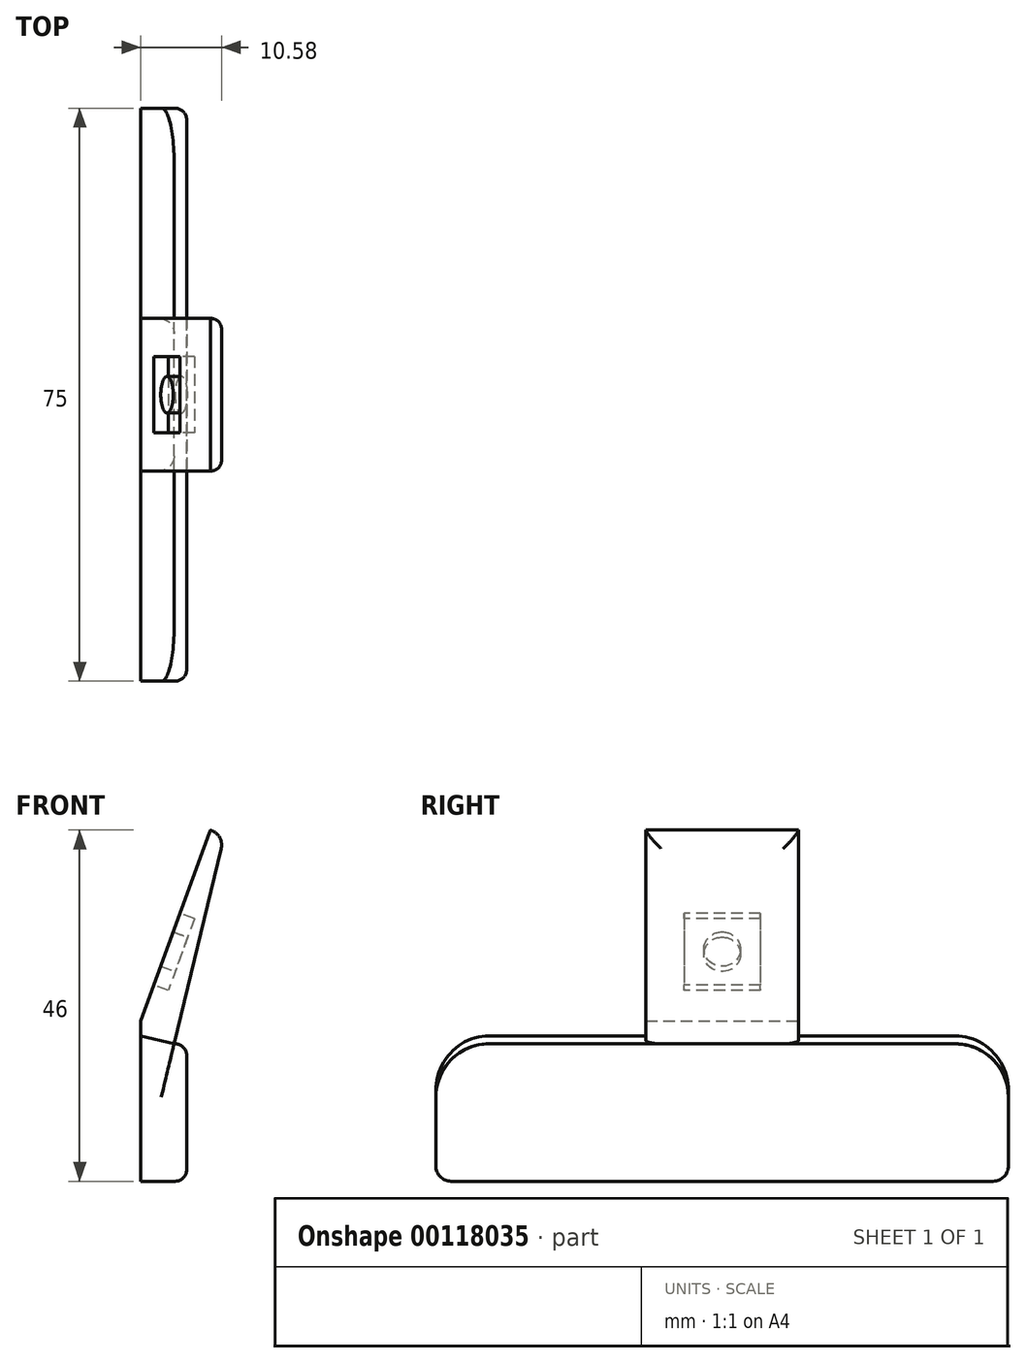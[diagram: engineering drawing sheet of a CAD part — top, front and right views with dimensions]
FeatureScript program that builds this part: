
annotation { "Feature Type Name" : "Feature", "Feature Type Description" : "" }
export const myFeature = defineFeature(function(context is Context, id is Id, definition is map)
    precondition{}
    {
        {
            var Q0;
            Q0=qCreatedBy(makeId("Right.planeOp"),FACE);
            var sketch = newSketch(context, id + "F0", { "sketchPlane" : qUnion([Q0])});
            skLineSegment(sketch, "E0", {"start": v(35.5, 0) * mm, "end": v(-35.5, 0) * mm});
            skLineSegment(sketch, "E1", {"start": v(-37.5, 2) * mm, "end": v(-37.5, 11) * mm});
            skLineSegment(sketch, "E2", {"start": v(-30.5, 18) * mm, "end": v(30.5, 18) * mm});
            skLineSegment(sketch, "E3", {"start": v(37.5, 11) * mm, "end": v(37.5, 2) * mm});
            skPoint(sketch, "E4.visualSharp", {"position": v(-37.5, 18) * mm});
            skArc(sketch, "E4.filletArc", {"start": v(-30.5, 18) * mm, "mid": v(-35.45, 15.95) * mm, "end": v(-37.5, 11) * mm});
            skPoint(sketch, "E5.visualSharp", {"position": v(37.5, 18) * mm});
            skArc(sketch, "E5.filletArc", {"start": v(37.5, 11) * mm, "mid": v(35.45, 15.95) * mm, "end": v(30.5, 18) * mm});
            skPoint(sketch, "E6.visualSharp", {"position": v(37.5, 0) * mm});
            skArc(sketch, "E6.filletArc", {"start": v(35.5, 0) * mm, "mid": v(36.91, 0.59) * mm, "end": v(37.5, 2) * mm});
            skPoint(sketch, "E7.visualSharp", {"position": v(-37.5, 0) * mm});
            skArc(sketch, "E7.filletArc", {"start": v(-37.5, 2) * mm, "mid": v(-36.91, 0.59) * mm, "end": v(-35.5, 0) * mm});
            skSolve(sketch);
        }
        {
            var Q0;
            Q0=makeQuery(id+"F0.imprint","IMPRINT",FACE,{"disambiguationData":[TD([[makeQuery(id+"F0.imprint","IMPRINT",EDGE,{"derivedFrom":sQuery(id+"F0.wireOp",EDGE,"E0")}),-1.0]])]});
            extrude(context, id + "F1", {"entities" : qUnion([Q0]), "depth" : 6 * mm});
        }
        {
            var Q0;
            Q0=makeQuery(id+"F1.opExtrude","CAP_EDGE",EDGE,{"disambiguationData":[OSD([sQuery(id+"F0.wireOp",EDGE,"E3")])],"isStart":false});
            fillet(context, id + "F2", {"entities" : qUnion([Q0]), "radius" : 1.5 * mm, "tangentPropagation" : true, "allowEdgeOverflow" : false});
        }
        {
            var Q0;
            Q0=makeQuery(id+"F1.opExtrude","SWEPT_FACE",FACE,{"disambiguationData":[OSD([sQuery(id+"F0.wireOp",EDGE,"E3")])]});
            var sketch = newSketch(context, id + "F3", { "sketchPlane" : qUnion([Q0])});
            skLineSegment(sketch, "E8", {"start": v(-9.1, 46) * mm, "end": v(-10.91, 45.15) * mm});
            skLineSegment(sketch, "E9", {"start": v(-10.91, 45.15) * mm, "end": v(0, 0) * mm});
            skLineSegment(sketch, "E10", {"start": v(0, 0) * mm, "end": v(0, 11) * mm});
            skLineSegment(sketch, "E11", {"start": v(0, 11) * mm, "end": v(0, 21) * mm});
            skLineSegment(sketch, "E12", {"start": v(-9.1, 46) * mm, "end": v(0, 21) * mm});
            skSolve(sketch);
        }
        {
            var Q0;
            {var subQ2=sQuery(id+"F3.wireOp",EDGE,"E8");Q0=makeQuery(id+"F3.imprint","IMPRINT",FACE,{"disambiguationData":[TD([[makeQuery(id+"F3.imprint","IMPRINT",EDGE,{"derivedFrom":subQ2}),1.0]])]});}
            var Q1;
            Q1=makeQuery(id+"F1.opExtrude","SWEPT_FACE",FACE,{"disambiguationData":[OSD([sQuery(id+"F0.wireOp",EDGE,"E1")])]});
            extrude(context, id + "F4", {"entities" : qUnion([Q0]), "operationType" : NewBodyOperationType.ADD, "endBound" : BoundingType.UP_TO_SURFACE, "oppositeDirection" : true, "endBoundEntityFace" : qUnion([Q1]), "depth" : 25 * mm});
        }
        {
            var Q0;
            Q0=makeQuery(id+"F4.opExtrude","SWEPT_FACE",FACE,{"disambiguationData":[OSD([sQuery(id+"F3.wireOp",EDGE,"E9")])]});
            var sketch = newSketch(context, id + "F5", { "sketchPlane" : qUnion([Q0])});
            skPoint(sketch, "E13.visualSharp", {"position": v(30.5, 11.32) * mm});
            skLineSegment(sketch, "E14", {"start": v(30.5, 18.52) * mm, "end": v(30.5, 18.52) * mm});
            skLineSegment(sketch, "E15", {"start": v(37.5, 11.52) * mm, "end": v(37.5, 11.32) * mm});
            skPoint(sketch, "E16.visualSharp", {"position": v(37.5, 18.52) * mm});
            skArc(sketch, "E16.filletArc", {"start": v(37.5, 11.52) * mm, "mid": v(35.45, 16.47) * mm, "end": v(30.5, 18.52) * mm});
            skLineSegment(sketch, "E17", {"start": v(37.5, 11.32) * mm, "end": v(37.5, 48.57) * mm});
            skLineSegment(sketch, "E18", {"start": v(37.5, 48.57) * mm, "end": v(10, 48.57) * mm});
            skLineSegment(sketch, "E19", {"start": v(10, 48.57) * mm, "end": v(10, 18.52) * mm});
            skLineSegment(sketch, "E20", {"start": v(10, 18.52) * mm, "end": v(30.5, 18.52) * mm});
            skLineSegment(sketch, "E21.MirrorCS", {"start": v(-37.5, 48.57) * mm, "end": v(-10, 48.57) * mm});
            skLineSegment(sketch, "E22.MirrorCS", {"start": v(-10, 48.57) * mm, "end": v(-10, 18.52) * mm});
            skLineSegment(sketch, "E23.MirrorCS", {"start": v(-10, 18.52) * mm, "end": v(-30.5, 18.52) * mm});
            skArc(sketch, "E24.MirrorCS", {"start": v(-37.5, 11.52) * mm, "mid": v(-35.45, 16.47) * mm, "end": v(-30.5, 18.52) * mm});
            skLineSegment(sketch, "E25.MirrorCS", {"start": v(-37.5, 11.32) * mm, "end": v(-37.5, 48.57) * mm});
            skSolve(sketch);
        }
        {
            var Q0;
            Q0 = qSketchRegion(id + "F5", true);
            extrude(context, id + "F6", {"entities" : qUnion([Q0]), "operationType" : NewBodyOperationType.REMOVE, "endBound" : BoundingType.THROUGH_ALL, "oppositeDirection" : true, "depth" : 25 * mm});
        }
        {
            var Q0;
            Q0=makeQuery(id+"F6.boolean.opBoolean","COPY",EDGE,{"derivedFrom":makeQuery(id+"F6.opExtrude","CAP_EDGE",EDGE,{"disambiguationData":[OSD([sQuery(id+"F5.wireOp",EDGE,"E19")])],"isStart":true})});
            var Q1;
            Q1=makeQuery(id+"F4.opExtrude","SWEPT_EDGE",EDGE,{"disambiguationData":[OSD([sQuery(id+"F3.wireOp",EDGE,"E8"),sQuery(id+"F3.wireOp",EDGE,"E9")])]});
            var Q2;
            Q2=makeQuery(id+"F6.boolean.opBoolean","COPY",EDGE,{"derivedFrom":makeQuery(id+"F6.opExtrude","CAP_EDGE",EDGE,{"disambiguationData":[OSD([sQuery(id+"F5.wireOp",EDGE,"E22.MirrorCS")])],"isStart":true})});
            fillet(context, id + "F7", {"entities" : qUnion([Q0, Q1, Q2]), "radius" : 2 * mm, "tangentPropagation" : true, "allowEdgeOverflow" : false});
        }
        {
            var Q0;
            Q0=makeQuery(id+"F4.opExtrude","SWEPT_FACE",FACE,{"disambiguationData":[OSD([sQuery(id+"F3.wireOp",EDGE,"E12")])]});
            var sketch = newSketch(context, id + "F8", { "sketchPlane" : qUnion([Q0])});
            skLineSegment(sketch, "E26.bottom", {"start": v(-5, 34.73) * mm, "end": v(5, 34.73) * mm});
            skLineSegment(sketch, "E26.top", {"start": v(-5, 24.73) * mm, "end": v(5, 24.73) * mm});
            skLineSegment(sketch, "E26.left", {"start": v(-5, 34.73) * mm, "end": v(-5, 24.73) * mm});
            skLineSegment(sketch, "E26.right", {"start": v(5, 34.73) * mm, "end": v(5, 24.73) * mm});
            skSolve(sketch);
        }
        {
            var Q0;
            Q0=makeQuery(id+"F8.imprint","IMPRINT",FACE,{"disambiguationData":[TD([[makeQuery(id+"F8.imprint","IMPRINT",EDGE,{"derivedFrom":sQuery(id+"F8.wireOp",EDGE,"E26.bottom")}),-1.0]])]});
            extrude(context, id + "F9", {"entities" : qUnion([Q0]), "operationType" : NewBodyOperationType.REMOVE, "oppositeDirection" : true, "depth" : 2 * mm});
        }
        {
            var Q0;
            Q0=makeQuery(id+"F9.boolean.opBoolean","COPY",FACE,{"derivedFrom":makeQuery(id+"F9.opExtrude","CAP_FACE",FACE,{"disambiguationData":[OSD([sQuery(id+"F8.wireOp",EDGE,"E26.bottom"),sQuery(id+"F8.wireOp",EDGE,"E26.top"),sQuery(id+"F8.wireOp",EDGE,"E26.left"),sQuery(id+"F8.wireOp",EDGE,"E26.right")])],"isStart":false})});
            var sketch = newSketch(context, id + "F10", { "sketchPlane" : qUnion([Q0])});
            skCircle(sketch, "E27", {"center": v(0, 29.73) * mm, "radius": 2.4 * mm});
            skSolve(sketch);
        }
        {
            var Q0;
            Q0=makeQuery(id+"F10.imprint","IMPRINT",FACE,{"disambiguationData":[TD([[makeQuery(id+"F10.imprint","IMPRINT",EDGE,{"derivedFrom":sQuery(id+"F10.wireOp",EDGE,"E27")}),1.0]])]});
            extrude(context, id + "F11", {"entities" : qUnion([Q0]), "operationType" : NewBodyOperationType.ADD, "depth" : 2 * mm});
        }
    });
